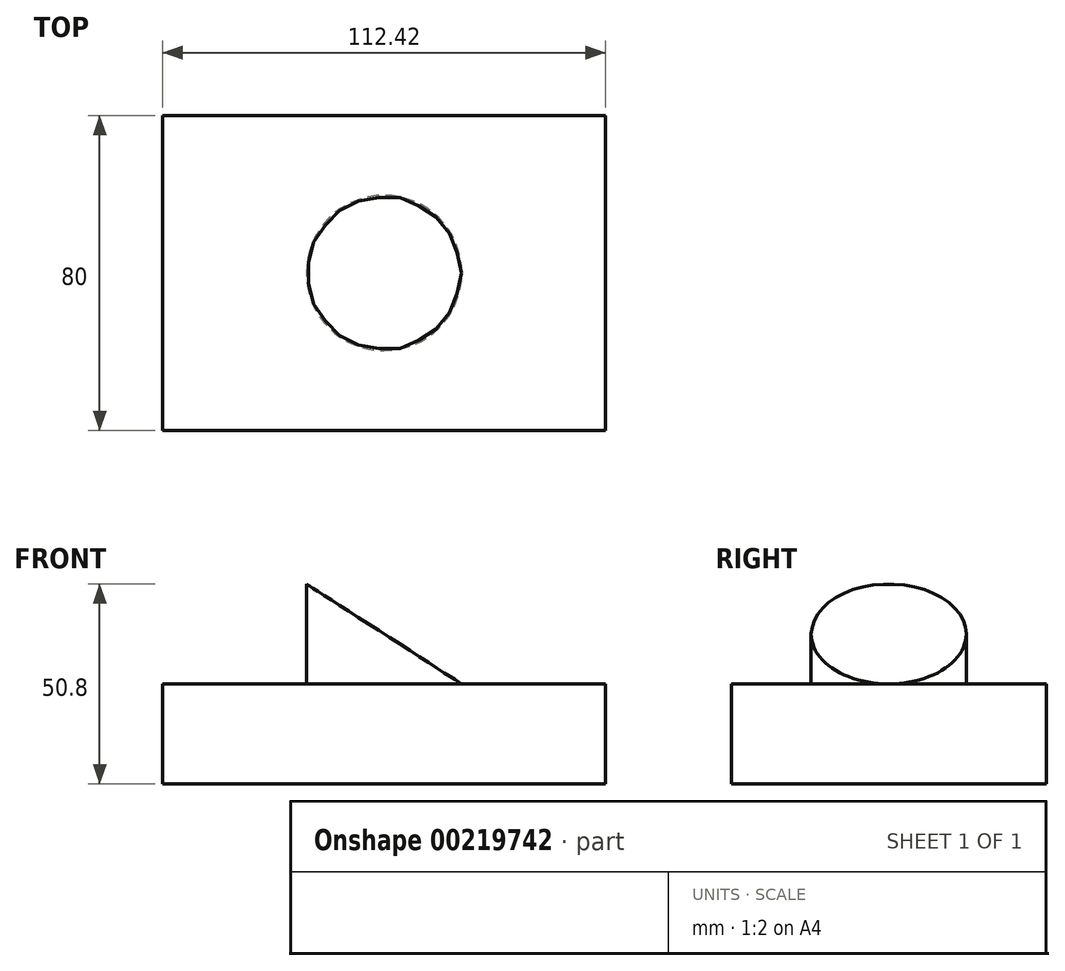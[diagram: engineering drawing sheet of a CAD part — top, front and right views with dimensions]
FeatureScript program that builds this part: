
annotation { "Feature Type Name" : "Feature", "Feature Type Description" : "" }
export const myFeature = defineFeature(function(context is Context, id is Id, definition is map)
    precondition{}
    {
        {
            var Q0;
            Q0=qCreatedBy(makeId("Top.planeOp"),FACE);
            var sketch = newSketch(context, id + "F0", { "sketchPlane" : qUnion([Q0])});
            skLineSegment(sketch, "E0.bottom", {"start": v(-56.21, 40) * mm, "end": v(56.21, 40) * mm});
            skLineSegment(sketch, "E0.top", {"start": v(-56.21, -40) * mm, "end": v(56.21, -40) * mm});
            skLineSegment(sketch, "E0.left", {"start": v(-56.21, 40) * mm, "end": v(-56.21, -40) * mm});
            skLineSegment(sketch, "E0.right", {"start": v(56.21, 40) * mm, "end": v(56.21, -40) * mm});
            skPoint(sketch, "E0.middle", {"position": v(0, 0) * mm});
            skSolve(sketch);
        }
        {
            var Q0;
            Q0 = qSketchRegion(id + "F0", true);
            extrude(context, id + "F1", {"entities" : qUnion([Q0]), "depth" : 25.4 * mm});
        }
        {
            var Q0;
            Q0=qCreatedBy(makeId("Top.planeOp"),FACE);
            var sketch = newSketch(context, id + "F2", { "sketchPlane" : qUnion([Q0])});
            skCircle(sketch, "E1", {"center": v(0, 0) * mm, "radius": 19.72 * mm});
            skSolve(sketch);
        }
        {
            var Q0;
            Q0 = qSketchRegion(id + "F2", true);
            extrude(context, id + "F3", {"entities" : qUnion([Q0]), "operationType" : NewBodyOperationType.ADD, "depth" : 50.8 * mm});
        }
        {
            var Q0;
            Q0=makeQuery(id+"F1.opExtrude","SWEPT_FACE",FACE,{"disambiguationData":[OSD([sQuery(id+"F0.wireOp",EDGE,"E0.top")])]});
            var sketch = newSketch(context, id + "F4", { "sketchPlane" : qUnion([Q0])});
            skLineSegment(sketch, "E2.0", {"start": v(-19.72, 50.8) * mm, "end": v(19.72, 50.8) * mm});
            skLineSegment(sketch, "E3", {"start": v(19.72, 50.8) * mm, "end": v(19.72, 25.4) * mm});
            skLineSegment(sketch, "E4", {"start": v(-19.72, 50.8) * mm, "end": v(19.72, 25.4) * mm});
            skSolve(sketch);
        }
        {
            var Q0;
            Q0 = qSketchRegion(id + "F4", true);
            extrude(context, id + "F5", {"entities" : qUnion([Q0]), "operationType" : NewBodyOperationType.REMOVE, "endBound" : BoundingType.THROUGH_ALL, "oppositeDirection" : true, "depth" : 25.4 * mm});
        }
    });
